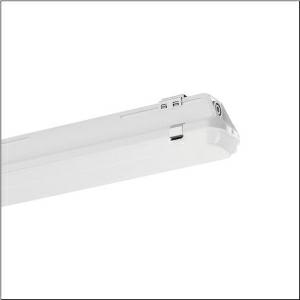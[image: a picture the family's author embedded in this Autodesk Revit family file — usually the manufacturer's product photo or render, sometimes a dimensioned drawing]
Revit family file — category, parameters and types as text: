
# Revit family: monsun_11_51fp22mp4b0u
name_source: partatom
category: Lighting Fixtures
units: mm (PartAtom-declared; Revit-internal decimal feet)

## family parameters
Cut with Voids When Loaded = No
Host = Face
Light Source = No
Part Type = Normal
Room Calculation Point = No
Round Connector Dimension = Use Diameter
Shared = No

## types (1)
- --- (1 x LED, 10520 lm, 62.4 W, 4000K)
    Apparent Load = 62 VA
    CIE Flux Codes = 49 78 94 96 100
    Color Rendering = 80
    Color Temperature = 4000K
    Default Elevation = 1800 mm
    Description = Monsun 11, damp-proof luminaire, chain hanger, primary light control with lens, primary optical cover: enclosure, of PC, light emission: direct distribution, primary light characteristic: symmetric, installation type: suspended mounting, surface-mounted, horizontal mounting, vertical mounting, LED, rated luminous flux: 10.520lm, luminous efficacy: 167lm/W, light colour: 840, colour temperature: 4000K, control gear: ON/OFF Multilumen, with terminal, 3-pole, max. 2.5mm², mains connection: 220..240V, AC, 50/60Hz, rated input power: 62W, luminaire housing, of glass-fibre reinforced polyester, uncoated, bright grey, incl. chain hanger, length: 1.590mm, width: 90mm, height: 88mm, clip for enclosure, of stainless steel (V2A), ceiling mounting element, of stainless steel (V2A), chain hanger, of stainless steel (V2A), protection rating (complete): IP66, insulation class (complete): insulation class I (protective earthing), certification: CE, ENEC, VDE, UKCA, protection symbol: D, impact resistance: IK08, permissible operating ambient temperature: -35..+35°C, standard: EN 50419, EN 60598-2-1, contact your sales advisor before using the luminaires in applications with unclear chemical exposure, large temperature fluctuations or condensation-forming humidity, LABS conformity tested according to VDMA 24364:2018-05, no direct snow, no direct sun, no direct rain, for indoor or canopied outdoor use, corresponds to IFS (International Featured Standards) requirements for safety and quality in the food industry, packaging unit: 1 piece
    Height = 89 mm
    Lamp = 1 x LED
    Lamp Light Flux = 10520 lm
    Lamp Power = 62.4 W
    Lamp count = 1
    Length = 1590 mm
    Luminous efficacy = 169 lm/W
    Manufacturer = Siteco
    ModVariant = No
    Model = 51FP22MP4B0U
    Mounting Place = Ceiling
    Mounting Type = Surface mounted
    Number of Poles = 1
    OnlyDefault = Yes
    Power Factor = 1
    Product Name = Monsun 11
    Product group = damp-proof luminaire
    ProductGroupID = 300
    Protection Class = Protection class I
    Protection Degree = IP 66
    RLX_Detail_Level = 1
    RLX_Emergency_Light_Flux = 0 lm
    RLX_Emergency_Type = 0
    RLX_Emergency_Type_DB = No
    RlxData = <blob elided: 90013 chars, md5=872beecc>
    Socket = socket
    Standby Power = 0 W
    System Light Flux = 10520 lm
    System Power = 62 W
    Type Comments = factory setting: luminous flux: 100 % | (A | C | E) | 147 mA
    Type Image = l_1349237.jpg
    URL = http://relux.com
    VarID = @adj_000017
    Voltage = 0 V
    Weight = 0.00 kg
    Width = 90 mm

## geometry (parser evidence)
native form markers: Blend x4, Sweep x10
no freeform markers — native parametric forms only
